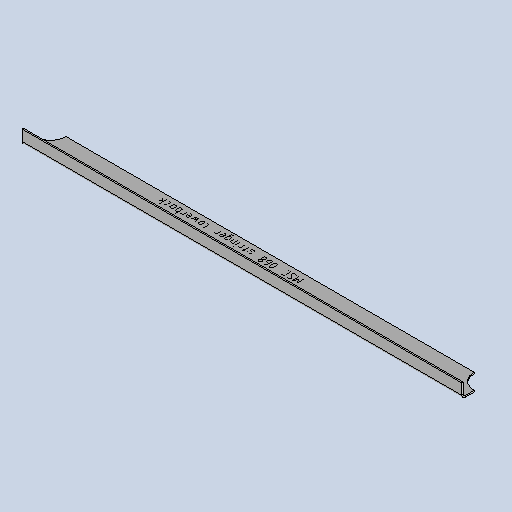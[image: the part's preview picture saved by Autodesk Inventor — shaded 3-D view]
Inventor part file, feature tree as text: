
AUTODESK INVENTOR PART (.ipt)
format: ipt  version: 2025 (Build 290162010, 162A)  size: 375,808 bytes
history: native  units: mm
features: other x5, sketch x5, sheet_metal_op x4, extrude x2, projected_geometry x1
ambient origin geometry x8: Origin, YZ Plane, XZ Plane, XY Plane, X Axis, Y Axis, Z Axis, Center Point
bodies: Solid1 (feature_tree)
feature tree (17):
  sheet_metal_op  "Face1"
  sheet_metal_op  "Flange1"
  extrude  "Extrusion2"  Depth=2.0mm
  other  "Mark2"
  other  "A-Side Definition"
  extrude  "Extrusion4"  Depth=2.0mm
  sketch  "Sketch1"  dims[d1=40.0mm d2=2.0mm]
  other  "Plate1"
  sketch  "Sketch2"  dims[d3=2.0mm d4=1.0mm]
  other  "Plate2"
  sheet_metal_op  "Bend1"
  sheet_metal_op  "Corner1"
  sketch  "Sketch6"  dims[d5=4.0mm]
  sketch  "Sketch9"  dims[d6=2.75mm]
  sketch  "Sketch10"  dims[d7=20.0mm d8=90.0deg d9=2.75mm d10=8.0mm d11=2.0mm d12=2.75mm d24=45.0mm d25=30.0mm d26=0.0mm d40=200.0mm d41=12.0mm d42=5.0mm d43=5.0mm d45=625.0mm d46=45.0mm d47=0.0mm d48=0.0mm]
  projected_geometry  "Projected Loop4"
  other  "Definition1"
